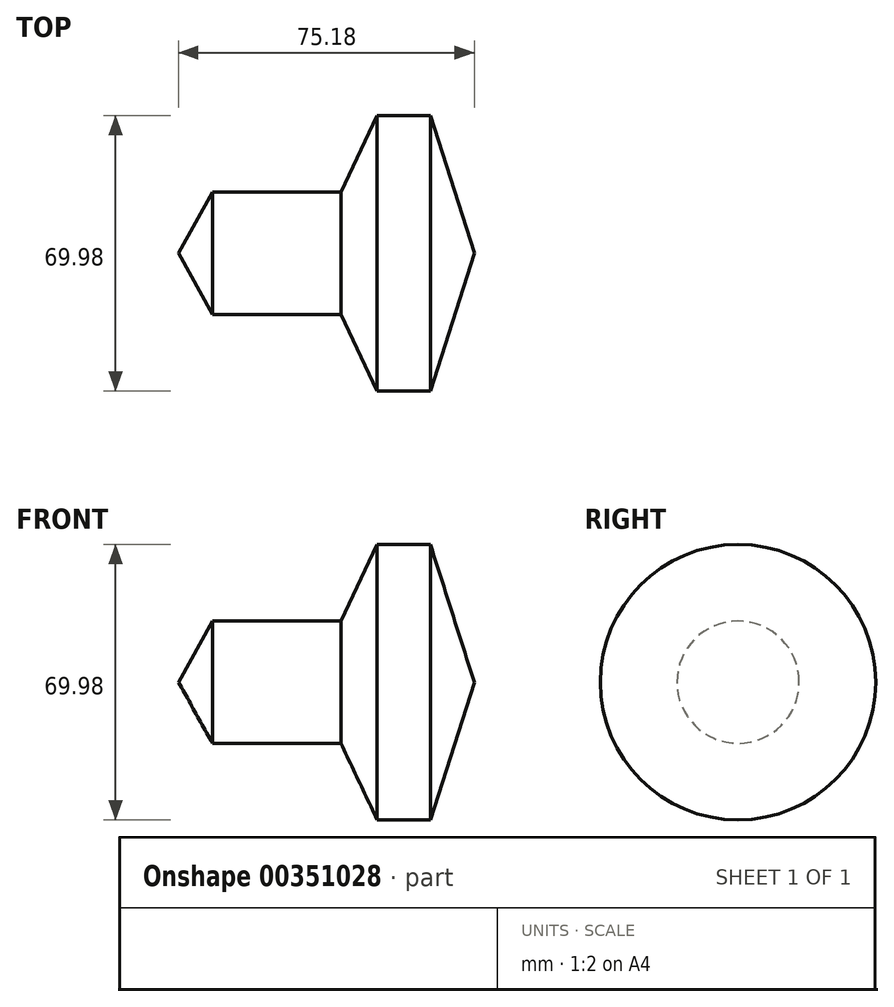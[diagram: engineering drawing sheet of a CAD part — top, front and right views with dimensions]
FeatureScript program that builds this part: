
annotation { "Feature Type Name" : "Feature", "Feature Type Description" : "" }
export const myFeature = defineFeature(function(context is Context, id is Id, definition is map)
    precondition{}
    {
        {
            var Q0;
            Q0=qCreatedBy(makeId("Front.planeOp"),FACE);
            var sketch = newSketch(context, id + "F0", { "sketchPlane" : qUnion([Q0])});
            skLineSegment(sketch, "E0", {"start": v(0, 0) * mm, "end": v(8.68, 15.52) * mm});
            skLineSegment(sketch, "E1", {"start": v(8.68, 15.52) * mm, "end": v(41.25, 15.52) * mm});
            skLineSegment(sketch, "E2", {"start": v(41.25, 15.52) * mm, "end": v(50.5, 34.99) * mm});
            skLineSegment(sketch, "E3", {"start": v(50.5, 34.99) * mm, "end": v(64, 34.99) * mm});
            skLineSegment(sketch, "E4", {"start": v(64, 34.99) * mm, "end": v(75.18, 0) * mm});
            skLineSegment(sketch, "E5", {"start": v(75.18, 0) * mm, "end": v(0, 0) * mm});
            skSolve(sketch);
        }
        {
            var Q0;
            Q0=makeQuery(id+"F0.imprint","IMPRINT",FACE,{"disambiguationData":[TD([[makeQuery(id+"F0.imprint","IMPRINT",EDGE,{"derivedFrom":sQuery(id+"F0.wireOp",EDGE,"E0")}),-1.0]])]});
            var Q1;
            Q1=sQuery(id+"F0.wireOp",EDGE,"E5");
            revolve(context, id + "F1", {"entities" : qUnion([Q0]), "axis" : qUnion([Q1]), "revolveType" : RevolveType.FULL});
        }
    });
